# Revit family: OTLO
name_source: partatom
category: Lighting Fixtures
units: mm (PartAtom-declared; Revit-internal decimal feet)

## family parameters
Always vertical = Yes
Cut with Voids When Loaded = No
Host = Ceiling
Light Source = Yes
OmniClass Number = 23.80.70.11
OmniClass Title = Luminaries for Internal Lighting
Part Type = Normal
Room Calculation Point = No
Round Connector Dimension = Use Diameter
Shared = No

## types (2) — shared parameters
Acoustic Tile = Acoustic Ceiling Tile 24 x 24
Assembly Code = D5020200
Color Filter = 16777215
Description = LED Troffer Dish Outline Type O
Dimming Lamp Color Temperature Shift = <None>
Emit Shape Visible in Rendering = No
Emit from Rectangle Length = 1' - 11 3/4"
Emit from Rectangle Width = 1' - 11 3/4"
Housing Finish = Metal - Viscor - White
Lamp = LED
Length = 1' - 11 3/4"
Lens Finish = Polycarbonate - Viscor - Frosted Flat
Manufacturer = VISIONEERING by VISCOR
Model = OTLO
Tilt Angle = 90.00°
URL = https://www.viscor.com
Voltage = 120 V
Width = 1' - 11 3/4"

## per-type parameters (varying)
| type | Apparent Load | Lamp Wattage | Photometric Web File |
| OTLO2X2-LED840K020LUNV | 19 VA | 19 VA | OTLO2X2-LED840K020LUNV.ies |
| OTLO2X2-LED840K040LUNV | 36 VA | 36 VA | OTLO2X2-LED840K040LUNV-G003822.IES |

## geometry (parser evidence)
native form markers: Sweep x2
no freeform markers — native parametric forms only
